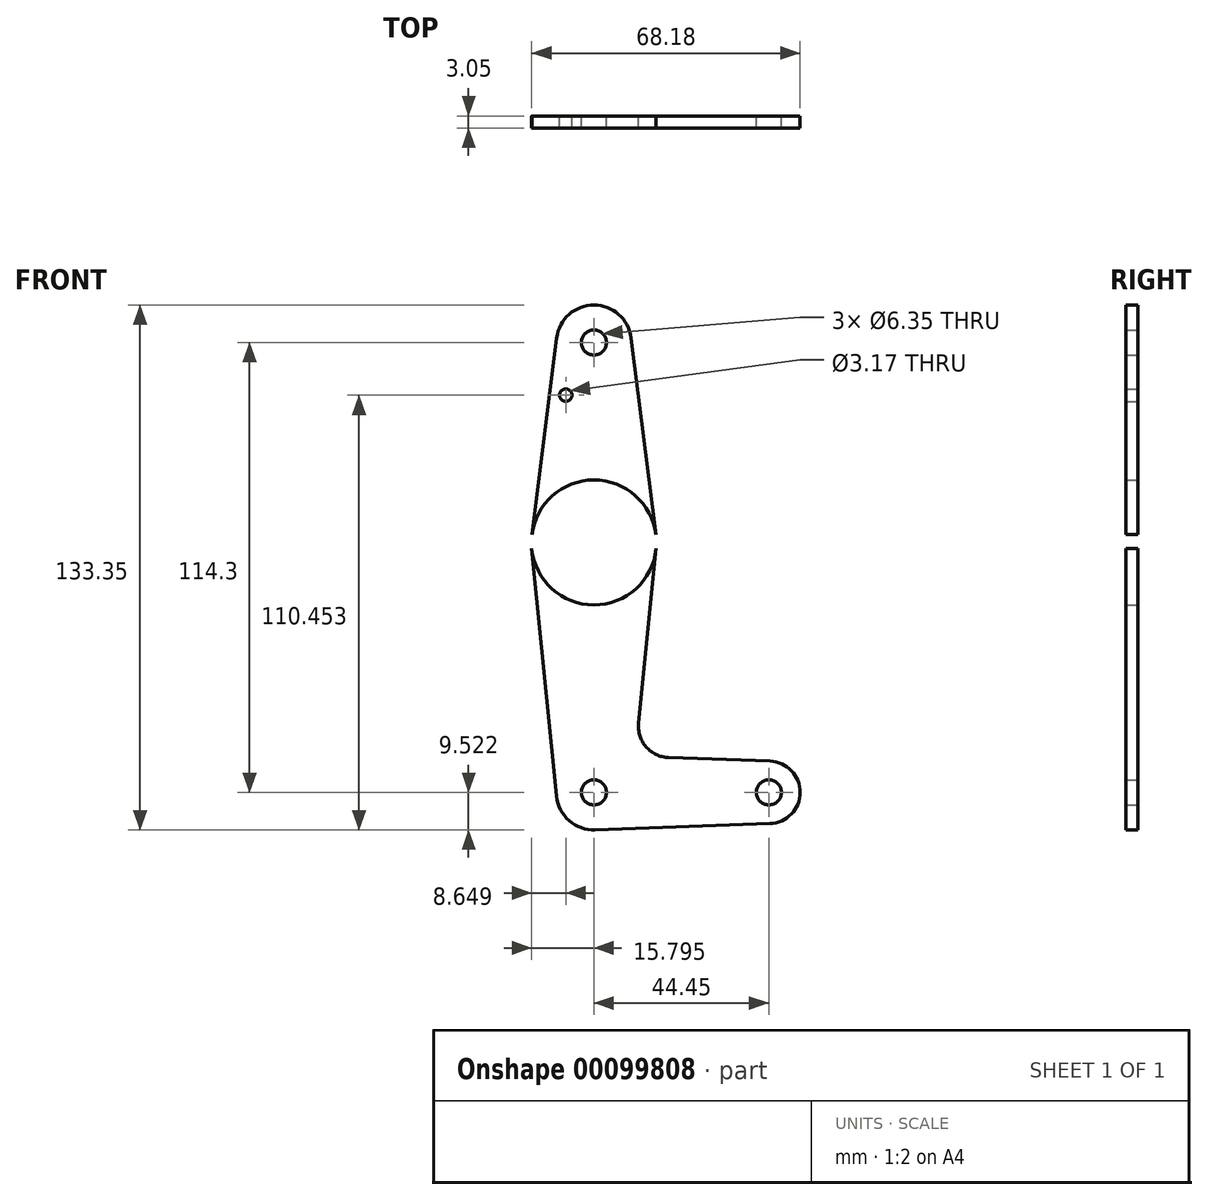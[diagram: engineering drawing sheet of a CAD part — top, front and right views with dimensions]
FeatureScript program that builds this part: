
annotation { "Feature Type Name" : "Feature", "Feature Type Description" : "" }
export const myFeature = defineFeature(function(context is Context, id is Id, definition is map)
    precondition{}
    {
        {
            var Q0;
            Q0=qCreatedBy(makeId("Front.planeOp"),FACE);
            var sketch = newSketch(context, id + "F0", { "sketchPlane" : qUnion([Q0])});
            skLineSegment(sketch, "E0", {"start": v(19.66, 99.33) * mm, "end": v(19.66, -14.97) * mm});
            skCircle(sketch, "E1", {"center": v(19.66, 99.33) * mm, "radius": 9.53 * mm});
            skCircle(sketch, "E2", {"center": v(19.66, 48.53) * mm, "radius": 15.88 * mm});
            skCircle(sketch, "E3", {"center": v(19.66, -14.97) * mm, "radius": 9.53 * mm});
            skLineSegment(sketch, "E4", {"start": v(29.1, 100.52) * mm, "end": v(35.4, 50.52) * mm});
            skLineSegment(sketch, "E5", {"start": v(10.2, 100.52) * mm, "end": v(3.9, 50.52) * mm});
            skLineSegment(sketch, "E6", {"start": v(3.86, 46.94) * mm, "end": v(10.18, -15.92) * mm});
            skLineSegment(sketch, "E7", {"start": v(35.45, 46.94) * mm, "end": v(31, 2.63) * mm});
            skLineSegment(sketch, "E8", {"start": v(19.66, -14.97) * mm, "end": v(64.1, -14.97) * mm});
            skCircle(sketch, "E9", {"center": v(64.1, -14.97) * mm, "radius": 7.94 * mm});
            skLineSegment(sketch, "E10", {"start": v(20, -24.49) * mm, "end": v(64.39, -22.9) * mm});
            skLineSegment(sketch, "E11", {"start": v(38.62, -6.12) * mm, "end": v(64.39, -7.04) * mm});
            skCircle(sketch, "E12", {"center": v(19.66, 99.33) * mm, "radius": 3.18 * mm});
            skCircle(sketch, "E13", {"center": v(19.66, 48.53) * mm, "radius": 3.18 * mm});
            skCircle(sketch, "E14", {"center": v(12.5, 85.96) * mm, "radius": 1.59 * mm});
            skCircle(sketch, "E15", {"center": v(19.66, -14.97) * mm, "radius": 3.18 * mm});
            skCircle(sketch, "E16", {"center": v(64.1, -14.97) * mm, "radius": 3.18 * mm});
            skArc(sketch, "E17.filletArc", {"start": v(31, 2.63) * mm, "mid": v(32.92, -3.4) * mm, "end": v(38.62, -6.12) * mm});
            skSolve(sketch);
        }
        {
            var Q0;
            {var subQ0=sQuery(id+"F0.wireOp",EDGE,"E2");var subQ3=sQuery(id+"F0.wireOp",EDGE,"E0");var subQ4=makeQuery(id+"F0.imprint","INTERSECT",VERTEX,{"disambiguationData":[OD(0.0)],"derivedFrom":[subQ3,subQ0]});Q0=makeQuery(id+"F0.imprint","IMPRINT",FACE,{"disambiguationData":[TD([[makeQuery(id+"F0.imprint","IMPRINT",EDGE,{"disambiguationData":[TD([[subQ4,-1.0]])],"derivedFrom":subQ3}),-1.0]])]});}
            var Q1;
            {var subQ5=sQuery(id+"F0.wireOp",EDGE,"E4");Q1=makeQuery(id+"F0.imprint","IMPRINT",FACE,{"disambiguationData":[TD([[makeQuery(id+"F0.imprint","IMPRINT",EDGE,{"derivedFrom":subQ5}),-1.0]])]});}
            var Q2;
            {var subQ5=sQuery(id+"F0.wireOp",EDGE,"E6");Q2=makeQuery(id+"F0.imprint","IMPRINT",FACE,{"disambiguationData":[TD([[makeQuery(id+"F0.imprint","IMPRINT",EDGE,{"derivedFrom":subQ5}),1.0]])]});}
            var Q3;
            {var subQ0=sQuery(id+"F0.wireOp",EDGE,"E10");Q3=makeQuery(id+"F0.imprint","IMPRINT",FACE,{"disambiguationData":[TD([[makeQuery(id+"F0.imprint","IMPRINT",EDGE,{"derivedFrom":subQ0}),1.0]])]});}
            var Q4;
            Q4=makeQuery(id+"F0.imprint","IMPRINT",FACE,{"disambiguationData":[TD([[makeQuery(id+"F0.imprint","IMPRINT",EDGE,{"derivedFrom":sQuery(id+"F0.wireOp",EDGE,"E12")}),-1.0]])]});
            var Q5;
            {var subQ0=sQuery(id+"F0.wireOp",EDGE,"E2");var subQ2=sQuery(id+"F0.wireOp",EDGE,"E0");var subQ5=makeQuery(id+"F0.imprint","INTERSECT",VERTEX,{"disambiguationData":[OD(0.0)],"derivedFrom":[subQ2,subQ0]});Q5=makeQuery(id+"F0.imprint","IMPRINT",FACE,{"disambiguationData":[TD([[makeQuery(id+"F0.imprint","IMPRINT",EDGE,{"disambiguationData":[TD([[subQ5,-1.0]])],"derivedFrom":subQ2}),1.0]])]});}
            var Q6;
            {var subQ0=sQuery(id+"F0.wireOp",EDGE,"E5");Q6=makeQuery(id+"F0.imprint","IMPRINT",FACE,{"disambiguationData":[TD([[makeQuery(id+"F0.imprint","IMPRINT",EDGE,{"derivedFrom":subQ0}),1.0]])]});}
            var Q7;
            {var subQ0=sQuery(id+"F0.wireOp",EDGE,"E3");var subQ7=sQuery(id+"F0.wireOp",EDGE,"E0");var subQ8=makeQuery(id+"F0.imprint","INTERSECT",VERTEX,{"derivedFrom":[subQ7,subQ0]});Q7=makeQuery(id+"F0.imprint","IMPRINT",FACE,{"disambiguationData":[TD([[makeQuery(id+"F0.imprint","IMPRINT",EDGE,{"disambiguationData":[TD([[subQ8,-1.0]])],"derivedFrom":subQ7}),-1.0]])]});}
            var Q8;
            Q8=makeQuery(id+"F0.imprint","IMPRINT",FACE,{"disambiguationData":[TD([[makeQuery(id+"F0.imprint","IMPRINT",EDGE,{"derivedFrom":sQuery(id+"F0.wireOp",EDGE,"E16")}),-1.0]])]});
            var Q9;
            {var subQ0=sQuery(id+"F0.wireOp",EDGE,"E7");Q9=makeQuery(id+"F0.imprint","IMPRINT",FACE,{"disambiguationData":[TD([[makeQuery(id+"F0.imprint","IMPRINT",EDGE,{"derivedFrom":subQ0}),-1.0]])]});}
            var Q10;
            {var subQ0=sQuery(id+"F0.wireOp",EDGE,"E3");var subQ1=sQuery(id+"F0.wireOp",EDGE,"E0");var subQ2=makeQuery(id+"F0.imprint","INTERSECT",VERTEX,{"derivedFrom":[subQ1,subQ0]});Q10=makeQuery(id+"F0.imprint","IMPRINT",FACE,{"disambiguationData":[TD([[makeQuery(id+"F0.imprint","IMPRINT",EDGE,{"disambiguationData":[TD([[subQ2,-1.0]])],"derivedFrom":subQ1}),1.0]])]});}
            extrude(context, id + "F1", {"entities" : qUnion([Q0, Q1, Q2, Q3, Q4, Q5, Q6, Q7, Q8, Q9, Q10]), "depth" : 3.05 * mm});
        }
    });
